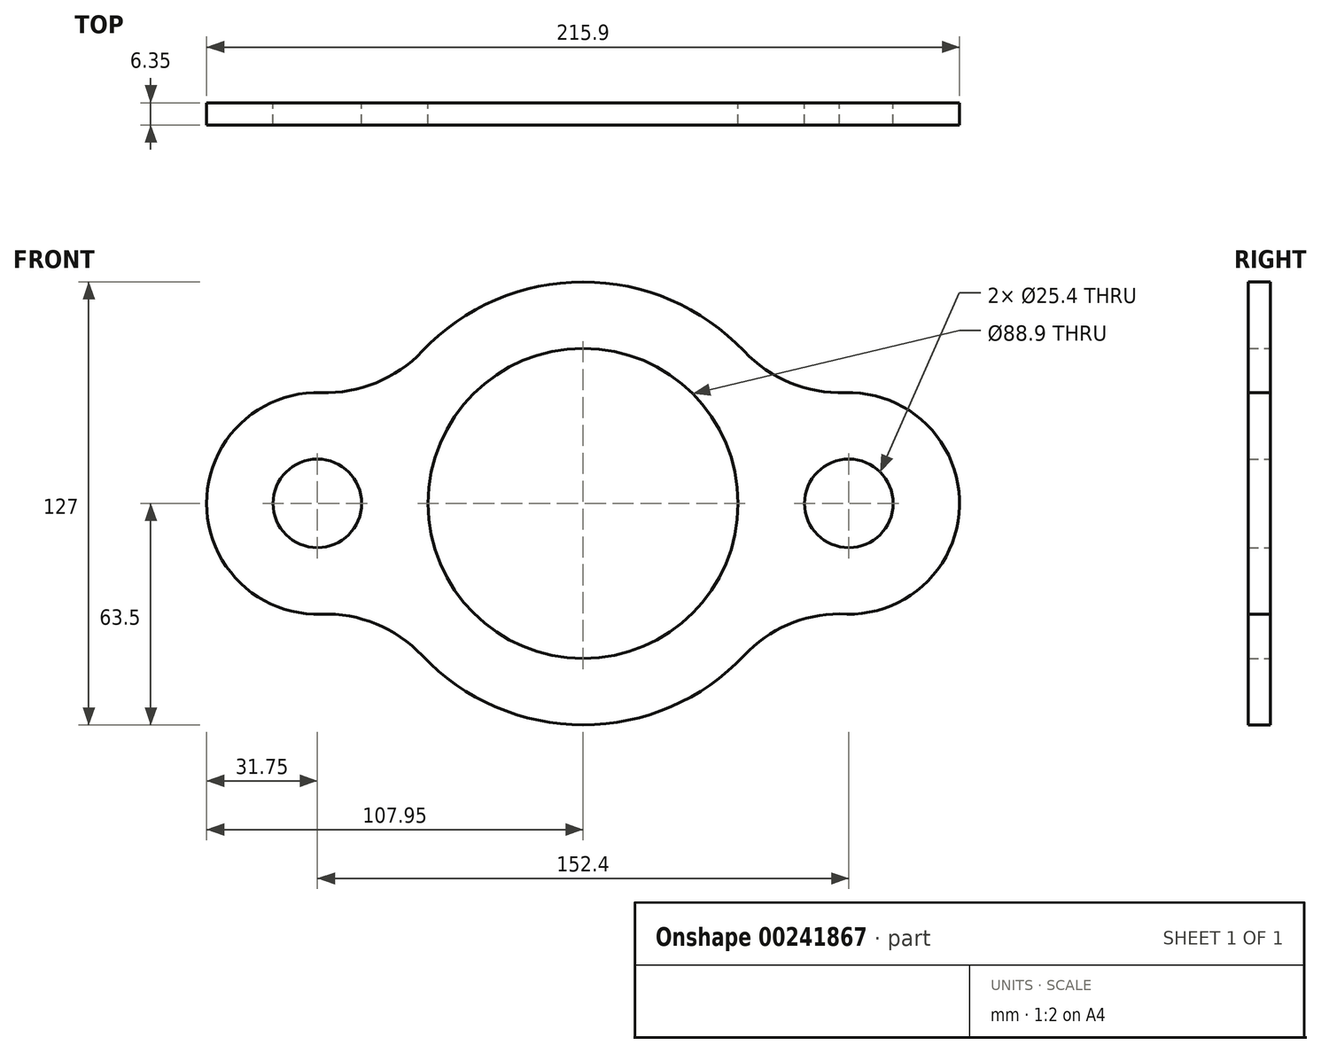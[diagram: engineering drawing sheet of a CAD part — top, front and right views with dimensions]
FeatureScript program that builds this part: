
annotation { "Feature Type Name" : "Feature", "Feature Type Description" : "" }
export const myFeature = defineFeature(function(context is Context, id is Id, definition is map)
    precondition{}
    {
        {
            var Q0;
            Q0=qCreatedBy(makeId("Front.planeOp"),FACE);
            var sketch = newSketch(context, id + "F0", { "sketchPlane" : qUnion([Q0])});
            skCircle(sketch, "E0", {"center": v(0, 0) * mm, "radius": 44.45 * mm});
            skCircle(sketch, "E1", {"center": v(-76.2, 0) * mm, "radius": 12.7 * mm});
            skCircle(sketch, "E2", {"center": v(76.2, 0) * mm, "radius": 12.7 * mm});
            skArc(sketch, "E3", {"start": v(-46.17, -43.6) * mm, "mid": v(0.01, -63.5) * mm, "end": v(46.2, -43.57) * mm});
            skArc(sketch, "E4", {"start": v(-75.1, 31.73) * mm, "mid": v(-107.95, -0.01) * mm, "end": v(-75.08, -31.73) * mm});
            skArc(sketch, "E5", {"start": v(73.5, -31.63) * mm, "mid": v(107.94, -0.81) * mm, "end": v(75.12, 31.73) * mm});
            skArc(sketch, "E6.trimOffspring", {"start": v(46.14, 43.63) * mm, "mid": v(-0.01, 63.5) * mm, "end": v(-46.15, 43.62) * mm});
            skArc(sketch, "E7", {"start": v(46.14, 43.63) * mm, "mid": v(59.35, 34.56) * mm, "end": v(75.12, 31.73) * mm});
            skArc(sketch, "E8", {"start": v(73.5, -31.63) * mm, "mid": v(58.63, -34.82) * mm, "end": v(46.2, -43.57) * mm});
            skArc(sketch, "E9", {"start": v(-46.17, -43.6) * mm, "mid": v(-59.35, -34.55) * mm, "end": v(-75.08, -31.73) * mm});
            skArc(sketch, "E10", {"start": v(-75.1, 31.73) * mm, "mid": v(-59.35, 34.56) * mm, "end": v(-46.15, 43.62) * mm});
            skSolve(sketch);
        }
        {
            var Q0;
            Q0=makeQuery(id+"F0.imprint","IMPRINT",FACE,{"disambiguationData":[TD([[makeQuery(id+"F0.imprint","IMPRINT",EDGE,{"derivedFrom":sQuery(id+"F0.wireOp",EDGE,"E0")}),-1.0]])]});
            extrude(context, id + "F1", {"entities" : qUnion([Q0]), "depth" : 6.35 * mm});
        }
    });
